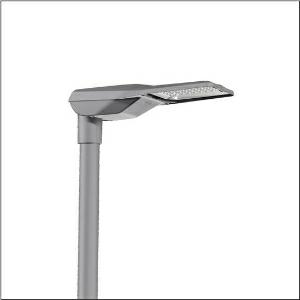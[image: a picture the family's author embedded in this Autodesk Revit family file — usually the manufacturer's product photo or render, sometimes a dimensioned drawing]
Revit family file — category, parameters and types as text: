
# Revit family: streetlight_sl_21_iq_mini___stw1_0a_5xe2e31d08hb_6dd6
name_source: partatom
category: Lighting Fixtures
units: mm (PartAtom-declared; Revit-internal decimal feet)

## family parameters
Cut with Voids When Loaded = No
Host = Face
Light Source = No
Part Type = Normal
Room Calculation Point = No
Round Connector Dimension = Use Diameter
Shared = No

## types (1)
- --- (1 x LED, 9450 lm, 70.9 W, 3000K)
    Apparent Load = 71 VA
    CIE Flux Codes = 38 75 98 100 100
    Color Rendering = 70
    Color Temperature = 3000K
    Default Elevation = 1800 mm
    Description = Streetlight SL 21 iQ mini, mast luminaire, primary light control with lens, of PMMA, primary optical cover: cover, of toughened safety glass, transparent, light distribution: STW1.0a, light emission: direct distribution, primary light characteristic: asymmetric, installation type: post-top, side-entry, LED, High Power LED, rated luminous flux: 9.450lm, luminous efficacy: 133lm/W, light colour: 730, colour temperature: 3000K, control gear: iQ-Comfort, control: Auto-Match, Temp-Guard, Lumen-Switch, Night-Set, Smart-Wire, Light-Fading, Desk-Remote (wireless, voltage-free reading and setting of iQ features in the workshop via application-optimized NFC function/RFID function), optimised constant luminous flux control (CLO 2.0), pre-setting: linear dimming characteristic, mains connection: 220..240V, AC, 50/60Hz, start of lifetime: 71W, end of service life: 75W, reduction: 31W, luminaire housing, of diecast aluminium, powder-coated, SITECO metallic grey (DB 702S), corrosivity category C5 high according to DIN EN ISO 12944, please order mast flange separately, inclination adjustable: 0°, 5°, 10°, 15°, sealing non-destructively replaceable, multi-level sealing system, length: 628mm, width: 235mm, height: 110mm, mast flange for spigot size: 42mm (side-entry): 5XC10008XM4, 60/48mm (side-entry/post-top): 5XC10108XM2, 76/60mm (side-entry/post-top): 5XC10108XM1, mounting height: 4..8m, protection rating (complete): IP66, insulation class (complete): insulation class II (safety insulation), certification: CE, ENEC, ENEC+, VDE, impact resistance: IK10, permissible operating ambient temperature for outdoor applications: -40..+50°C, standard-compliant lighting for roads and squares, packaging unit: 1 piece

Light Distribution: STW1.0a
    Height = 110 mm
    Lamp = 1 x LED
    Lamp Light Flux = 9450 lm
    Lamp Power = 70.9 W
    Lamp count = 1
    Length = 625 mm
    Luminous efficacy = 133 lm/W
    Manufacturer = Siteco
    ModVariant = No
    Model = 5XE2E31D08HB
    Number of Poles = 1
    OnlyDefault = Yes
    Power Factor = 1
    Product Name = Streetlight SL 21 iQ mini | STW1.0a
    Product group = mast luminaire | pylon top
    ProductGroupID = 6100
    Protection Class = Protection class II
    Protection Degree = IP 66
    RLX_Detail_Level = 1
    RLX_Emergency_Light_Flux = 0 lm
    RLX_Emergency_Type = 0
    RLX_Emergency_Type_DB = No
    RlxData = <blob elided: 26381 chars, md5=a2e67f78>
    Socket = socket
    Standby Power = 0 W
    System Light Flux = 9450 lm
    System Power = 71 W
    Type Comments = factory setting: luminous flux: 100 % | dim-lin: 254 | 711 mA
    Type Image = l_1003519.jpg
    URL = http://relux.com
    VarID = @adj_157337
    Voltage = 0 V
    Weight = 0.00 kg
    Width = 234 mm

## geometry (parser evidence)
native form markers: Blend x4, Sweep x10
no freeform markers — native parametric forms only
